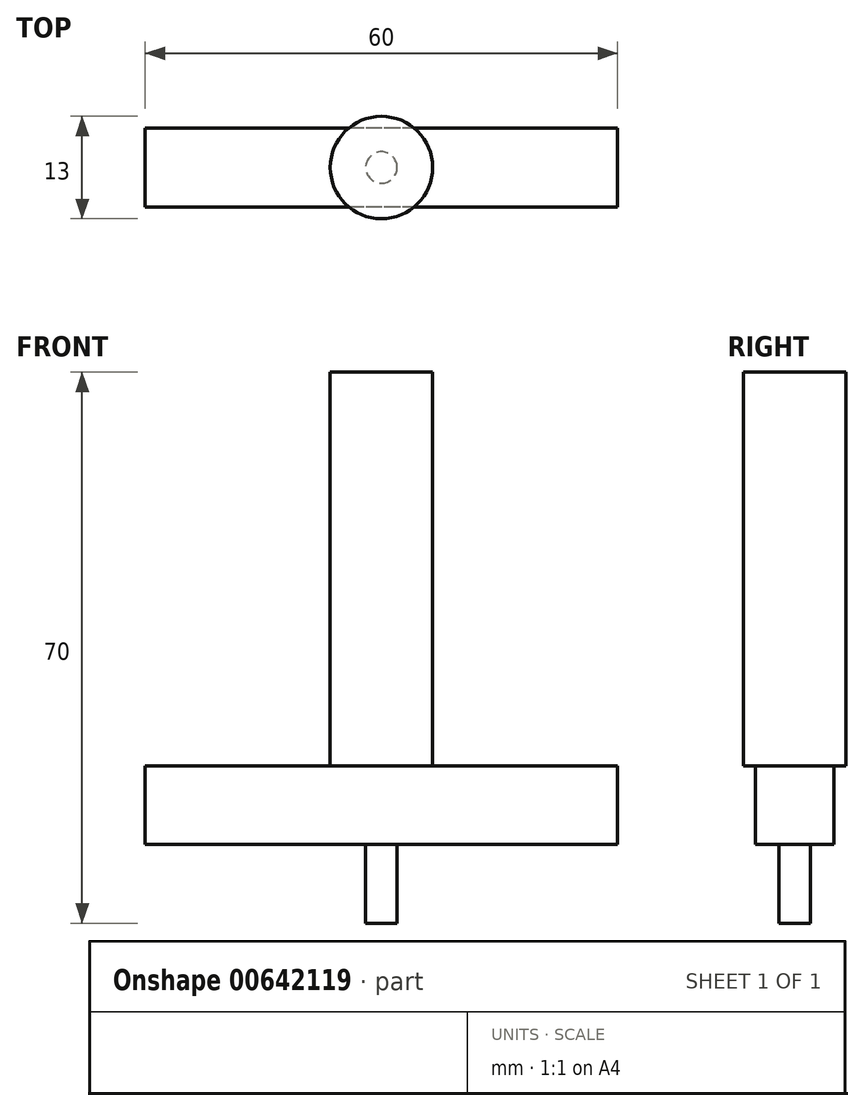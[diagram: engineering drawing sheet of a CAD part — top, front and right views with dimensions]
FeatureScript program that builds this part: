
annotation { "Feature Type Name" : "Feature", "Feature Type Description" : "" }
export const myFeature = defineFeature(function(context is Context, id is Id, definition is map)
    precondition{}
    {
        {
            var Q0;
            Q0=qCreatedBy(makeId("Front.planeOp"),FACE);
            var sketch = newSketch(context, id + "F0", { "sketchPlane" : qUnion([Q0])});
            skLineSegment(sketch, "E0", {"start": v(0, 50) * mm, "end": v(0, 0) * mm});
            skSolve(sketch);
        }
        {
            var Q0;
            Q0=qCreatedBy(makeId("Top.planeOp"),FACE);
            var sketch = newSketch(context, id + "F1", { "sketchPlane" : qUnion([Q0])});
            skCircle(sketch, "E1", {"center": v(0, 0) * mm, "radius": 6.5 * mm});
            skSolve(sketch);
        }
        {
            var Q0;
            Q0=makeQuery(id+"F1.imprint","IMPRINT",FACE,{"disambiguationData":[TD([[makeQuery(id+"F1.imprint","IMPRINT",EDGE,{"derivedFrom":sQuery(id+"F1.wireOp",EDGE,"E1")}),1.0]])]});
            var Q1;
            Q1=sQuery(id+"F0.wireOp",EDGE,"E0");
            sweep(context, id + "F2", {"profiles" : qUnion([Q0]), "path" : qUnion([Q1])});
        }
        {
            var Q0;
            Q0=qCreatedBy(makeId("Top.planeOp"),FACE);
            var sketch = newSketch(context, id + "F3", { "sketchPlane" : qUnion([Q0])});
            skLineSegment(sketch, "E2.bottom", {"start": v(30, -5) * mm, "end": v(-30, -5) * mm});
            skLineSegment(sketch, "E2.top", {"start": v(30, 5) * mm, "end": v(-30, 5) * mm});
            skLineSegment(sketch, "E2.left", {"start": v(30, -5) * mm, "end": v(30, 5) * mm});
            skLineSegment(sketch, "E2.right", {"start": v(-30, -5) * mm, "end": v(-30, 5) * mm});
            skPoint(sketch, "E2.middle", {"position": v(0, 0) * mm});
            skSolve(sketch);
        }
        {
            var Q0;
            Q0=makeQuery(id+"F3.imprint","IMPRINT",FACE,{"disambiguationData":[TD([[makeQuery(id+"F3.imprint","IMPRINT",EDGE,{"derivedFrom":sQuery(id+"F3.wireOp",EDGE,"E2.bottom")}),-1.0]])]});
            extrude(context, id + "F4", {"entities" : qUnion([Q0]), "operationType" : NewBodyOperationType.ADD, "oppositeDirection" : true, "depth" : 10 * mm, "offsetDistance" : 25 * mm});
        }
        {
            var Q0;
            Q0=qCreatedBy(makeId("Top.planeOp"),FACE);
            var sketch = newSketch(context, id + "F5", { "sketchPlane" : qUnion([Q0])});
            skCircle(sketch, "E3", {"center": v(0, 0) * mm, "radius": 2 * mm});
            skSolve(sketch);
        }
        {
            var Q0;
            Q0 = qSketchRegion(id + "F5", true);
            extrude(context, id + "F6", {"entities" : qUnion([Q0]), "operationType" : NewBodyOperationType.ADD, "oppositeDirection" : true, "depth" : 20 * mm, "offsetDistance" : 25 * mm});
        }
    });
